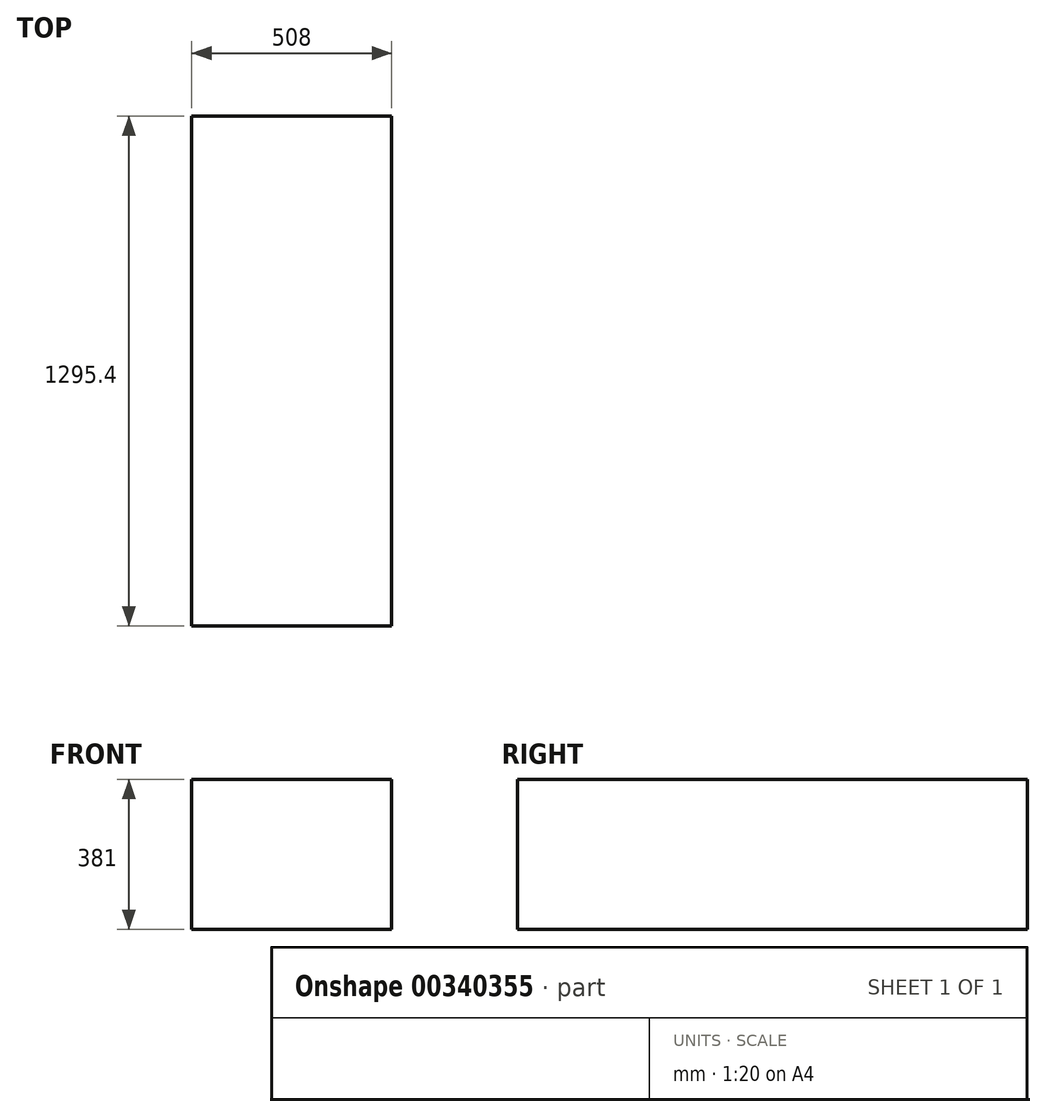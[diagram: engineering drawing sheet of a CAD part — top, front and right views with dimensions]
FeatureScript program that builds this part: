
annotation { "Feature Type Name" : "Feature", "Feature Type Description" : "" }
export const myFeature = defineFeature(function(context is Context, id is Id, definition is map)
    precondition{}
    {
        {
            var Q0;
            Q0=qCreatedBy(makeId("Front.planeOp"),FACE);
            var sketch = newSketch(context, id + "F0", { "sketchPlane" : qUnion([Q0])});
            skLineSegment(sketch, "E0.bottom", {"start": v(-400.02, -14.34) * mm, "end": v(107.98, -14.34) * mm});
            skLineSegment(sketch, "E0.top", {"start": v(-400.02, -395.34) * mm, "end": v(107.98, -395.34) * mm});
            skLineSegment(sketch, "E0.left", {"start": v(-400.02, -14.34) * mm, "end": v(-400.02, -395.34) * mm});
            skLineSegment(sketch, "E0.right", {"start": v(107.98, -14.34) * mm, "end": v(107.98, -395.34) * mm});
            skSolve(sketch);
        }
        {
            var Q0;
            Q0=makeQuery(id+"F0.imprint","IMPRINT",FACE,{"disambiguationData":[TD([[makeQuery(id+"F0.imprint","IMPRINT",EDGE,{"derivedFrom":sQuery(id+"F0.wireOp",EDGE,"E0.bottom")}),-1.0]])]});
            extrude(context, id + "F1", {"entities" : qUnion([Q0]), "depth" : 1295.4 * mm});
        }
    });
